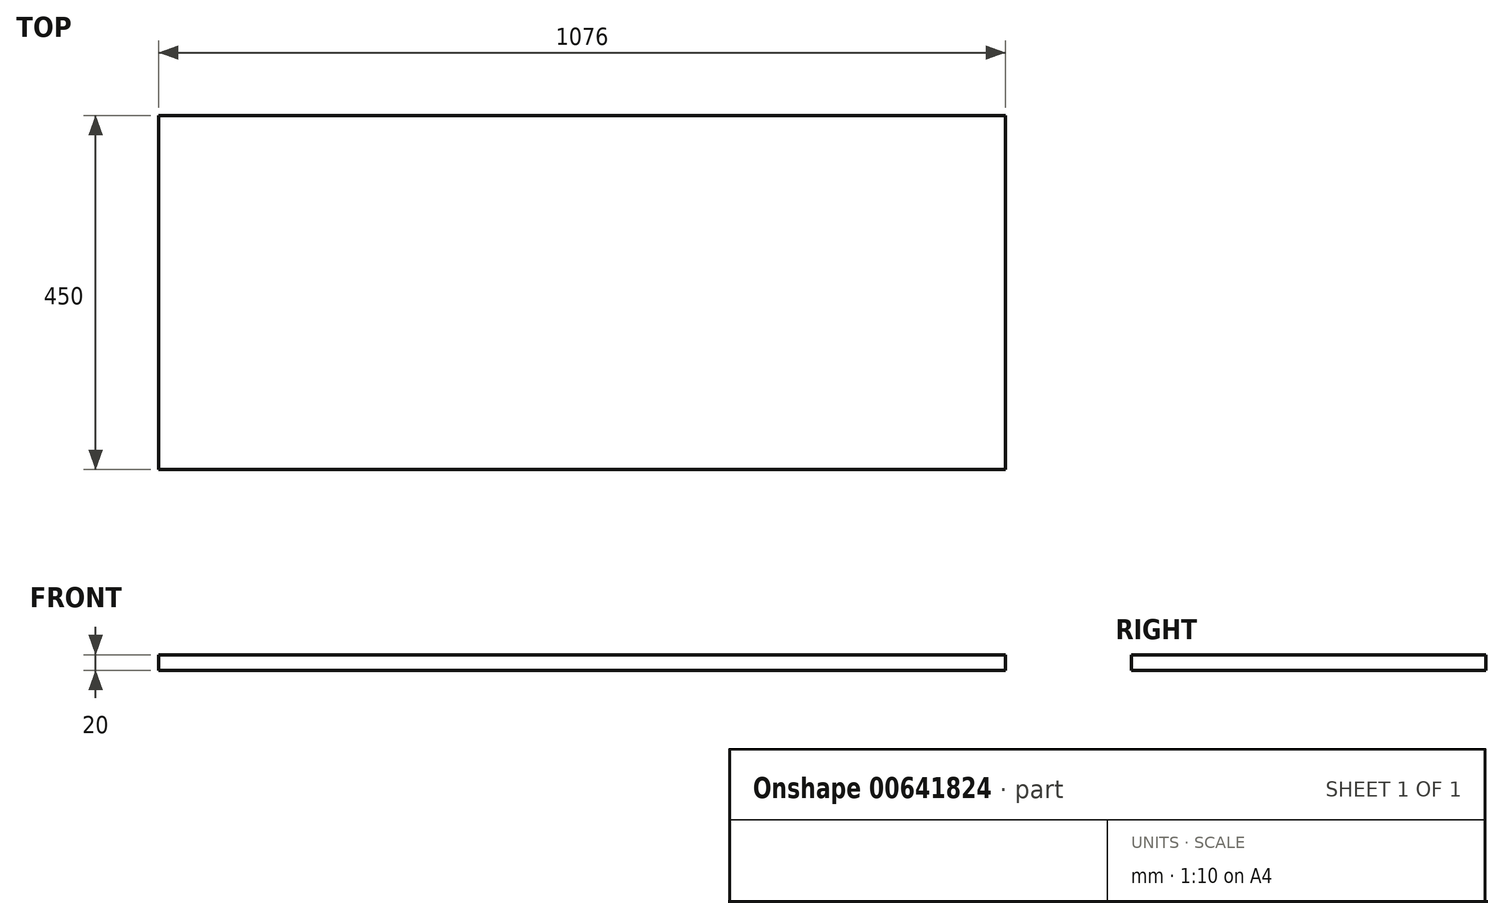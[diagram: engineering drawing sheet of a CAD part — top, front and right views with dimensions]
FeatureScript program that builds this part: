
annotation { "Feature Type Name" : "Feature", "Feature Type Description" : "" }
export const myFeature = defineFeature(function(context is Context, id is Id, definition is map)
    precondition{}
    {
        {
            var Q0;
            Q0=qCreatedBy(makeId("Top.planeOp"),FACE);
            var sketch = newSketch(context, id + "F0", { "sketchPlane" : qUnion([Q0])});
            skLineSegment(sketch, "E0", {"start": v(920.28, 444.23) * mm, "end": v(-155.72, 444.23) * mm});
            skLineSegment(sketch, "E1", {"start": v(-155.72, 444.23) * mm, "end": v(-155.72, -5.77) * mm});
            skLineSegment(sketch, "E2", {"start": v(-155.72, -5.77) * mm, "end": v(920.28, -5.77) * mm});
            skLineSegment(sketch, "E3", {"start": v(920.28, -5.77) * mm, "end": v(920.28, 444.23) * mm});
            skSolve(sketch);
        }
        {
            var Q0;
            Q0=makeQuery(id+"F0.imprint","IMPRINT",FACE,{"disambiguationData":[TD([[makeQuery(id+"F0.imprint","IMPRINT",EDGE,{"derivedFrom":sQuery(id+"F0.wireOp",EDGE,"E0")}),1.0]])]});
            extrude(context, id + "F1", {"entities" : qUnion([Q0]), "depth" : 20 * mm, "offsetDistance" : 25 * mm});
        }
    });
